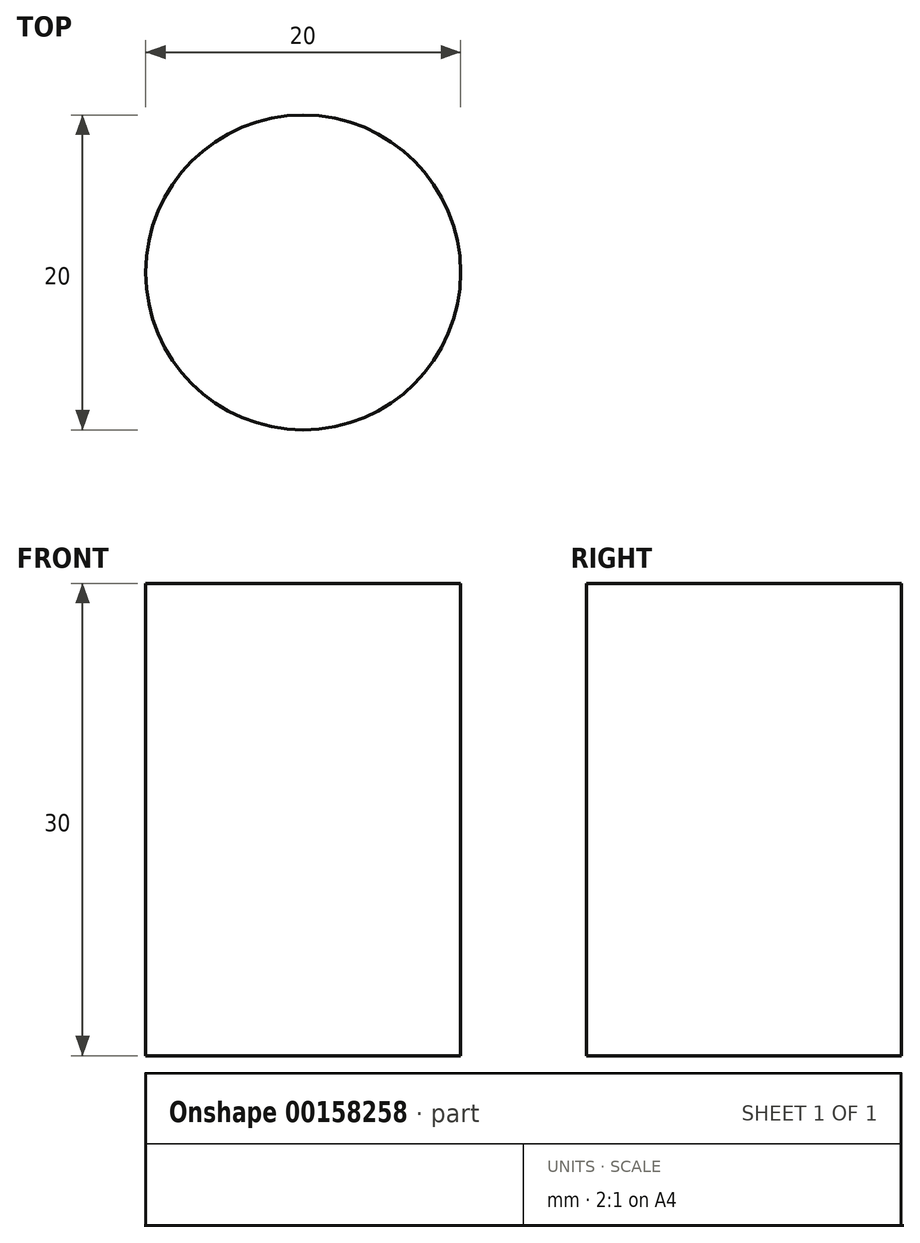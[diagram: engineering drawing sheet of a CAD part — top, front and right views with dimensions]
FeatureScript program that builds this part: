
annotation { "Feature Type Name" : "Feature", "Feature Type Description" : "" }
export const myFeature = defineFeature(function(context is Context, id is Id, definition is map)
    precondition{}
    {
        {
            var Q0;
            Q0=qCreatedBy(makeId("Top.planeOp"),FACE);
            var sketch = newSketch(context, id + "F0", { "sketchPlane" : qUnion([Q0])});
            skCircle(sketch, "E0", {"center": v(0, 0) * mm, "radius": 10 * mm});
            skSolve(sketch);
        }
        {
            var Q0;
            Q0=makeQuery(id+"F0.imprint","IMPRINT",FACE,{"disambiguationData":[TD([[makeQuery(id+"F0.imprint","IMPRINT",EDGE,{"derivedFrom":sQuery(id+"F0.wireOp",EDGE,"E0")}),1.0]])]});
            var Q1;
            Q1=sQuery(id+"F0.wireOp",EDGE,"E0");
            extrude(context, id + "F1", {"entities" : qUnion([Q0]), "surfaceEntities" : qUnion([Q1]), "depth" : 30 * mm});
        }
    });
